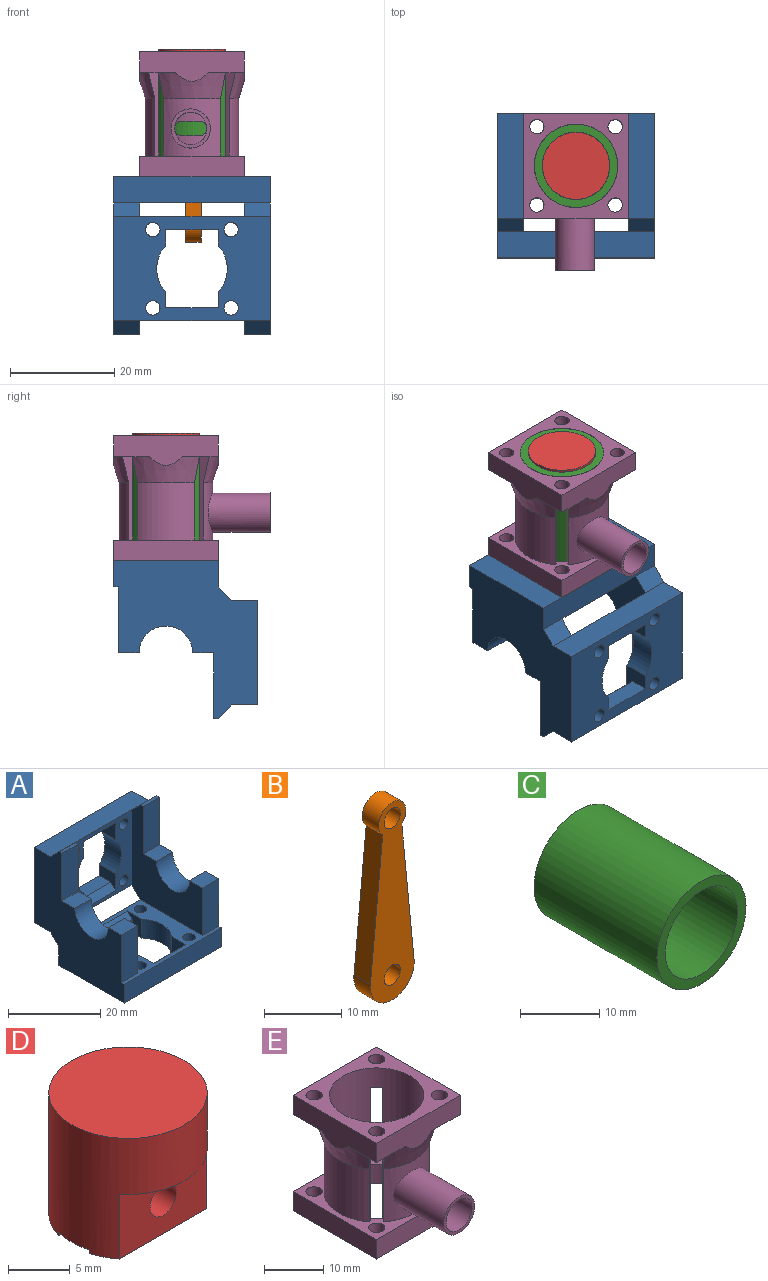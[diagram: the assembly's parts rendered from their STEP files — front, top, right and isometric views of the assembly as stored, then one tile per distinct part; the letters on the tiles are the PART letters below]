
ASSEMBLY  parts=5 mates=9
PART A: 56 faces, bbox 30x27.6x30.2 mm
  f0: plane 20x20mm, normal (0,-1,0), area 174.5mm2, adj f16,f27,f31,f32,f40,f41,f42,f43
  f1: plane 30x20mm, normal (0,1,0), area 404.5mm2, adj f21,f26,f31,f32,f40,f41,f42,f43
  f2: plane 30x20mm, normal (0,0,1), area 183.2mm2, adj f3,f4,f5,f7,f8,f9,f10,f11
  f3: plane 5x4.47mm, normal (1,0,0), area 16mm2, adj f2,f6,f15,f29,f55
  f4: plane 5x4.47mm, normal (-1,0,0), area 16mm2, adj f2,f6,f15,f28,f55
  f5: plane 5x4.47mm, normal (1,0,0), area 16mm2, adj f2,f12,f15,f29,f52
  f6: plane 10x3.5mm, normal (0,-1,0), area 35mm2, adj f3,f4,f15,f55
  f7: plane 5x4.47mm, normal (-1,0,0), area 16mm2, adj f2,f12,f15,f28,f52
  f8: plane 30x5mm, normal (0,-1,0), area 150mm2, adj f2,f15,f21,f26
  f9: cylinder r=1.38mm len=5mm, axis (0,0,-1), area 43.2mm2, adj f2,f15
  f10: cylinder r=1.38mm len=5mm, axis (0,0,-1), area 43.2mm2, adj f2,f15
  f11: cylinder r=1.38mm len=5mm, axis (0,0,-1), area 43.2mm2, adj f2,f15
  f12: plane 10x3.5mm, normal (0,1,0), area 35mm2, adj f5,f7,f15,f52
  f13: plane 30x5mm, normal (0,1,0), area 150mm2, adj f2,f15,f21,f26,f30,f38
  f14: cylinder r=1.38mm len=5mm, axis (0,0,-1), area 43.2mm2, adj f2,f15
  f15: plane 30x20mm, normal (0,0,-1), area 404.5mm2, adj f3,f4,f5,f6,f7,f8,f9,f10
  f16: plane 25.2x21.73mm, normal (1,0,0), area 269.5mm2, adj f0,f2,f17,f18,f19,f20,f36,f37
  f17: plane 5x4mm, normal (0,0,1), area 20mm2, adj f16,f20,f21,f36
  f18: plane 12.6x5mm, normal (0,-1,0), area 63mm2, adj f2,f16,f19,f21
  f19: plane 5x4mm, normal (0,0,1), area 20mm2, adj f16,f18,f20,f21
  f20: cylinder r=5.12mm len=10.25mm, axis (1,0,0), area 80.5mm2, adj f16,f17,f19,f21
  f21: plane 30.2x27.6mm, normal (-1,0,0), area 469.5mm2, adj f1,f2,f8,f13,f15,f17,f18,f19
  f22: plane 5x4mm, normal (0,0,1), area 20mm2, adj f23,f26,f27,f35
  f23: cylinder r=5.12mm len=10.25mm, axis (-1,0,0), area 80.5mm2, adj f22,f24,f26,f27
  f24: plane 5x4mm, normal (0,0,1), area 20mm2, adj f23,f25,f26,f27
  f25: plane 12.6x5mm, normal (0,-1,0), area 63mm2, adj f2,f24,f26,f27
  f26: plane 30.2x27.6mm, normal (1,0,0), area 469.5mm2, adj f1,f2,f8,f13,f15,f22,f23,f24
  f27: plane 25.2x21.73mm, normal (-1,0,0), area 269.5mm2, adj f0,f2,f22,f23,f24,f25,f30,f33
  f28: cylinder r=6.75mm len=9.07mm, axis (0,0,1), area 49.7mm2, adj f2,f4,f7,f15
  f29: cylinder r=6.75mm len=9.07mm, axis (0,0,1), area 49.7mm2, adj f2,f3,f5,f15
  f30: plane 5x2.6mm, normal (0,0.71,-0.71), area 18.4mm2, adj f13,f26,f27,f31
  f31: plane 30x5mm, normal (0,0,-1), area 150mm2, adj f0,f1,f21,f26,f30,f38
  f32: plane 30x5mm, normal (0,0,1), area 150mm2, adj f0,f1,f21,f26,f33,f37
  f33: plane 5x2.6mm, normal (0,0.71,0.71), area 18.4mm2, adj f26,f27,f32,f34
  f34: plane 5x0.88mm, normal (0,0,1), area 4.4mm2, adj f26,f27,f33,f35
  f35: plane 12.6x5mm, normal (0,-1,0), area 63mm2, adj f22,f26,f27,f34
  f36: plane 12.6x5mm, normal (0,-1,0), area 63mm2, adj f16,f17,f21,f39
  f37: plane 5x2.6mm, normal (0,0.71,0.71), area 18.4mm2, adj f16,f21,f32,f39
  f38: plane 5x2.6mm, normal (0,0.71,-0.71), area 18.4mm2, adj f13,f16,f21,f31
  f39: plane 5x0.88mm, normal (0,0,1), area 4.4mm2, adj f16,f21,f36,f37
  f40: cylinder r=1.38mm len=5mm, axis (0,1,0), area 43.2mm2, adj f0,f1
  f41: cylinder r=1.38mm len=5mm, axis (0,1,0), area 43.2mm2, adj f0,f1
  f42: plane 5x4.47mm, normal (1,0,0), area 16mm2, adj f0,f1,f43,f49,f54
  f43: cylinder r=6.75mm len=9.07mm, axis (0,1,0), area 49.7mm2, adj f0,f1,f42,f44
  f44: plane 5x4.47mm, normal (1,0,0), area 16mm2, adj f0,f1,f43,f45,f53
  f45: plane 10x3.5mm, normal (0,0,-1), area 35mm2, adj f1,f44,f46,f53
  f46: plane 5x4.47mm, normal (-1,0,0), area 16mm2, adj f0,f1,f45,f47,f53
  f47: cylinder r=6.75mm len=9.07mm, axis (0,1,0), area 49.7mm2, adj f0,f1,f46,f48
  f48: plane 5x4.47mm, normal (-1,0,0), area 16mm2, adj f0,f1,f47,f49,f54
  f49: plane 10x3.5mm, normal (0,0,1), area 35mm2, adj f1,f42,f48,f54
  f50: cylinder r=1.38mm len=5mm, axis (0,1,0), area 43.2mm2, adj f0,f1
  f51: cylinder r=1.38mm len=5mm, axis (0,1,0), area 43.2mm2, adj f0,f1
  f52: plane 10x1.5mm, normal (0,0.71,0.71), area 21.2mm2, adj f2,f5,f7,f12
  f53: plane 10x1.5mm, normal (0,-0.71,-0.71), area 21.2mm2, adj f0,f44,f45,f46
  f54: plane 10x1.5mm, normal (0,-0.71,0.71), area 21.2mm2, adj f0,f42,f48,f49
  f55: plane 10x1.5mm, normal (0,-0.71,0.71), area 21.2mm2, adj f2,f3,f4,f6
PART B: 8 faces, bbox 8x3x31.3 mm
  f0: cylinder r=4mm len=8mm, axis (0,1,0), area 40.1mm2, adj f1,f3,f6,f7
  f1: plane 22.57x3mm, normal (1,0,0.1), area 68mm2, adj f0,f2,f6,f7
  f2: cylinder r=2.5mm len=5mm, axis (0,1,0), area 35.5mm2, adj f1,f3,f6,f7
  f3: plane 22.57x3mm, normal (-1,0,0.1), area 68mm2, adj f0,f2,f6,f7
  f4: cylinder r=1.5mm len=3mm, axis (0,1,0), area 28.3mm2, adj f6,f7
  f5: cylinder r=1.5mm len=3mm, axis (0,1,0), area 28.3mm2, adj f6,f7
  f6: plane 31.25x8mm, normal (0,-1,0), area 161.4mm2, adj f0,f1,f2,f3,f4,f5
  f7: plane 31.25x8mm, normal (0,1,0), area 161.4mm2, adj f0,f1,f2,f3,f4,f5
PART C: 4 faces, bbox 16x22x16 mm
  f0: cylinder r=6.47mm len=22mm, axis (0,-1,0), area 895mm2, adj f2,f3
  f1: cylinder r=7.97mm len=22mm, axis (0,-1,0), area 1102.4mm2, adj f2,f3
  f2: plane 15.95x15.95mm, normal (0,1,0), area 68.1mm2, adj f0,f1
  f3: plane 15.95x15.95mm, normal (0,-1,0), area 68.1mm2, adj f0,f1
PART D: 15 faces, bbox 12.9x12.9x12 mm
  f0: cylinder r=6.42mm len=12.85mm, axis (0,0,1), area 400.9mm2, adj f1,f4,f5,f6,f8,f9,f11,f12
  f1: plane 12.36x2.28mm, normal (0,0,-1), area 25.9mm2, adj f0,f9,f13
  f2: plane 4.91x3.5mm, normal (-0.82,0,-0.57), area 20.9mm2, adj f8,f9,f10,f12
  f3: plane 4.91x3.5mm, normal (0.82,0,-0.57), area 20.9mm2, adj f8,f9,f10,f11
  f4: plane 12.36x4.68mm, normal (0,0,-1), area 42.6mm2, adj f0,f8
  f5: cylinder r=1.5mm len=4.68mm, axis (0,-1,0), area 43.2mm2, adj f0,f8
  f6: plane 12.85x12.85mm, normal (0,0,1), area 129.7mm2, adj f0
  f7: cylinder r=1.5mm len=3mm, axis (0,-1,0), area 21.4mm2, adj f9,f13
  f8: plane 12.36x6.71mm, normal (0,-1,0), area 46.9mm2, adj f0,f2,f3,f4,f5,f10
  f9: plane 12.36x6.71mm, normal (0,1,0), area 46.9mm2, adj f0,f1,f2,f3,f7,f10
  f10: cylinder r=3.38mm len=5.55mm, axis (0,-1,0), area 22.8mm2, adj f2,f3,f8,f9
  f11: plane 3.5x0.24mm, normal (0,0,-1), area 0.6mm2, adj f0,f3
  f12: plane 3.5x0.24mm, normal (0,0,-1), area 0.6mm2, adj f0,f2
  f13: plane 10.02x6.44mm, normal (0,-1,0), area 57.4mm2, adj f0,f1,f7,f14
  f14: plane 10.02x2.4mm, normal (0,0,-1), area 16.7mm2, adj f0,f13
PART E: 49 faces, bbox 21x30.5x24 mm
  f0: cylinder r=9mm len=6.25mm, axis (0,0,-1), area 7.7mm2, adj f42,f44,f45,f46
  f1: cylinder r=9mm len=6.25mm, axis (0,0,-1), area 7.7mm2, adj f42,f43,f44,f46
  f2: plane 6.8x6.8mm, normal (0,0,-1), area 15.6mm2, adj f10,f18,f26,f29,f30,f36,f38,f41
  f3: plane 6.8x6.8mm, normal (0,0,-1), area 15.6mm2, adj f10,f16,f20,f29,f34,f35,f38,f39
  f4: plane 6.8x6.8mm, normal (0,0,-1), area 15.6mm2, adj f10,f21,f24,f31,f33,f35,f39,f40
  f5: plane 20x20mm, normal (0,0,1), area 130.6mm2, adj f6,f7,f8,f9,f10,f11,f12,f13
  f6: plane 20x4mm, normal (-1,0,0), area 80mm2, adj f5,f7,f13,f15
  f7: plane 20x4mm, normal (0,-1,0), area 80mm2, adj f5,f6,f8,f15
  f8: plane 20x4mm, normal (1,0,0), area 80mm2, adj f5,f7,f13,f15
  f9: cylinder r=1.38mm len=4mm, axis (0,0,-1), area 34.6mm2, adj f5,f15
  f10: cylinder r=8mm len=24mm, axis (0,0,-1), area 1057.3mm2, adj f2,f3,f4,f5,f15,f16,f18,f20
  f11: cylinder r=1.38mm len=4mm, axis (0,0,-1), area 34.6mm2, adj f5,f15
  f12: cylinder r=1.38mm len=4mm, axis (0,0,-1), area 34.6mm2, adj f5,f15
  f13: plane 20x4mm, normal (0,1,0), area 80mm2, adj f5,f6,f8,f15
  f14: cylinder r=1.38mm len=4mm, axis (0,0,-1), area 34.6mm2, adj f5,f15
  f15: plane 20x20mm, normal (0,0,-1), area 175.2mm2, adj f6,f7,f8,f9,f10,f11,f12,f13
  f16: plane 16x1.98mm, normal (0.61,0.79,0), area 19.8mm2, adj f3,f5,f10,f17,f38
  f17: cylinder r=9mm len=11mm, axis (0,0,-1), area 129.8mm2, adj f5,f16,f18,f38
  f18: plane 16x1.98mm, normal (0.61,-0.79,0), area 19.8mm2, adj f2,f5,f10,f17,f38
  f19: cylinder r=9mm len=11mm, axis (0,0,-1), area 129.8mm2, adj f5,f20,f21,f39
  f20: plane 16x1.98mm, normal (-0.79,-0.61,0), area 19.8mm2, adj f3,f5,f10,f19,f39
  f21: plane 16x1.98mm, normal (0.79,-0.61,0), area 19.8mm2, adj f4,f5,f10,f19,f39
  f22: plane 16x1.98mm, normal (-0.61,-0.79,0), area 19.8mm2, adj f5,f10,f23,f28,f40
  f23: cylinder r=9mm len=11mm, axis (0,0,-1), area 129.8mm2, adj f5,f22,f24,f40
  f24: plane 16x1.98mm, normal (-0.61,0.79,0), area 19.8mm2, adj f4,f5,f10,f23,f40
  f25: plane 16x1.98mm, normal (0.79,0.61,0), area 19.8mm2, adj f5,f10,f27,f28,f41
  f26: plane 16x1.98mm, normal (-0.79,0.61,0), area 19.8mm2, adj f2,f5,f10,f27,f41
  f27: cylinder r=9mm len=11mm, axis (0,0,-1), area 84.5mm2, adj f5,f25,f26,f41,f47
  f28: plane 6.8x6.8mm, normal (0,0,-1), area 15.6mm2, adj f10,f22,f25,f30,f31,f32,f40,f41
  f29: plane 20x5.67mm, normal (-1,0,0), area 87.1mm2, adj f2,f3,f30,f35,f37,f38
  f30: plane 20x5.67mm, normal (0,-1,0), area 87.1mm2, adj f2,f28,f29,f31,f37,f41
  f31: plane 20x5.67mm, normal (1,0,0), area 87.1mm2, adj f4,f28,f30,f35,f37,f40
  f32: cylinder r=1.38mm len=4mm, axis (0,0,-1), area 34.6mm2, adj f28,f37
  f33: cylinder r=1.38mm len=4mm, axis (0,0,-1), area 34.6mm2, adj f4,f37
  f34: cylinder r=1.38mm len=4mm, axis (0,0,-1), area 34.6mm2, adj f3,f37
  f35: plane 20x5.67mm, normal (0,1,0), area 87.1mm2, adj f3,f4,f29,f31,f37,f39
  f36: cylinder r=1.38mm len=4mm, axis (0,0,-1), area 34.6mm2, adj f2,f37
  f37: plane 20x20mm, normal (0,0,1), area 175.2mm2, adj f10,f29,f30,f31,f32,f33,f34,f35
  f38: cone r=10.5mm half-angle=16.7deg, axis (0,0,1), area 59.3mm2, adj f2,f3,f16,f17,f18,f29
  f39: cone r=10.5mm half-angle=16.7deg, axis (0,0,1), area 59.3mm2, adj f3,f4,f19,f20,f21,f35
  f40: cone r=10.5mm half-angle=16.7deg, axis (0,0,1), area 59.3mm2, adj f4,f22,f23,f24,f28,f31
  f41: cone r=10.5mm half-angle=16.7deg, axis (0,0,1), area 59.3mm2, adj f2,f25,f26,f27,f28,f30
  f42: cylinder r=1.38mm len=2.75mm, axis (0,-1,0), area 4.6mm2, adj f0,f1,f10,f43,f45
  f43: plane 3.5x1.25mm, normal (0,0,1), area 3.5mm2, adj f1,f10,f42,f44
  f44: cylinder r=1.38mm len=2.75mm, axis (0,-1,0), area 4.5mm2, adj f0,f1,f10,f43,f45
  f45: plane 3.5x1.25mm, normal (0,0,-1), area 3.5mm2, adj f0,f10,f42,f44
  f46: cylinder r=3.12mm len=11.66mm, axis (0,-1,0), area 221.5mm2, adj f0,f1,f48
  f47: cylinder r=3.75mm len=11.94mm, axis (0,-1,0), area 268.8mm2, adj f27,f48
  f48: plane 7.5x7.5mm, normal (0,-1,0), area 13.5mm2, adj f46,f47
PLACE A rot(axis=(1,0,0),180deg) t=(0,20,0)mm
PLACE B rot(axis=(0.1,0.1,-0.99),90.5deg) t=(10.25,14.72,-8.55)mm
PLACE C rot(axis=(0.58,0.58,0.58),120deg) t=(10,10,2)mm
PLACE D rot(axis=(0,0,1),90deg) t=(10,10,24.41)mm
PLACE E at identity
MATE cylindrical B.f5 <-> D.f5  axis (1,0,0) through (10.25,10,15.75)mm
MATE cylindrical A.f10 <-> E.f9  axis (0,0,1) through (17.5,17.5,-5)mm
MATE planar C.f1 <-> E.f0  axis (0,0,1) through (10,10,24)mm
MATE planar A.f15 <-> E.f15  axis (0,0,1) through (25,0,0)mm
MATE slider D.f0 <-> C.f0  axis (0,0,1) through (10,10,18.41)mm
MATE planar B.f7 <-> D.f5  axis (1,0,0) through (11.75,12.89,0.89)mm
MATE cylindrical A.f14 <-> E.f12  axis (0,0,1) through (2.5,2.5,-5)mm
MATE parallel D.f13 <-> E.f31  axis (1,0,0) through (14.03,15.01,15.63)mm
MATE cylindrical C.f1 <-> E.f0  axis (0,0,-1) through (10,10,24)mm
